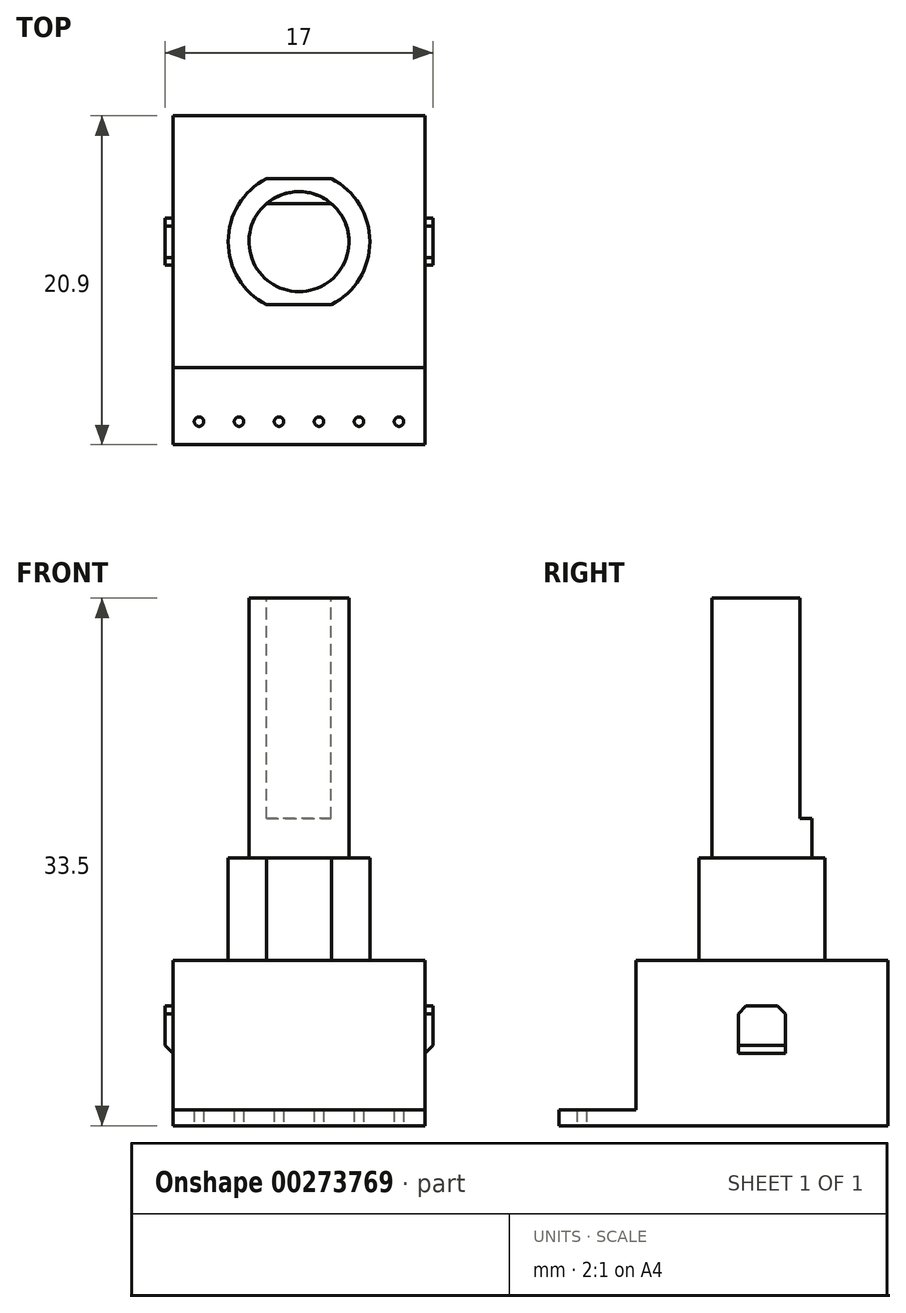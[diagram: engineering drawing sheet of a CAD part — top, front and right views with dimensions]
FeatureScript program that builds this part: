
annotation { "Feature Type Name" : "Feature", "Feature Type Description" : "" }
export const myFeature = defineFeature(function(context is Context, id is Id, definition is map)
    precondition{}
    {
        {
            var Q0;
            Q0=qCreatedBy(makeId("Top.planeOp"),FACE);
            var sketch = newSketch(context, id + "F0", { "sketchPlane" : qUnion([Q0])});
            skLineSegment(sketch, "E0.bottom", {"start": v(-8, 8) * mm, "end": v(8, 8) * mm});
            skLineSegment(sketch, "E0.top", {"start": v(-8, -12.9) * mm, "end": v(8, -12.9) * mm});
            skLineSegment(sketch, "E0.left", {"start": v(-8, 8) * mm, "end": v(-8, -12.9) * mm});
            skLineSegment(sketch, "E0.right", {"start": v(8, 8) * mm, "end": v(8, -12.9) * mm});
            skSolve(sketch);
        }
        {
            var Q0;
            Q0=makeQuery(id+"F0.imprint","IMPRINT",FACE,{"disambiguationData":[TD([[makeQuery(id+"F0.imprint","IMPRINT",EDGE,{"derivedFrom":sQuery(id+"F0.wireOp",EDGE,"E0.bottom")}),-1.0]])]});
            extrude(context, id + "F1", {"entities" : qUnion([Q0]), "depth" : 1 * mm});
        }
        {
            var Q0;
            Q0=makeQuery(id+"F1.opExtrude","CAP_FACE",FACE,{"disambiguationData":[OSD([sQuery(id+"F0.wireOp",EDGE,"E0.bottom"),sQuery(id+"F0.wireOp",EDGE,"E0.top"),sQuery(id+"F0.wireOp",EDGE,"E0.left"),sQuery(id+"F0.wireOp",EDGE,"E0.right")])],"isStart":false});
            var sketch = newSketch(context, id + "F2", { "sketchPlane" : qUnion([Q0])});
            skLineSegment(sketch, "E1.bottom", {"start": v(-8, 8) * mm, "end": v(8, 8) * mm});
            skLineSegment(sketch, "E1.top", {"start": v(-8, -8) * mm, "end": v(8, -8) * mm});
            skLineSegment(sketch, "E1.left", {"start": v(-8, 8) * mm, "end": v(-8, -8) * mm});
            skLineSegment(sketch, "E1.right", {"start": v(8, 8) * mm, "end": v(8, -8) * mm});
            skSolve(sketch);
        }
        {
            var Q0;
            Q0=makeQuery(id+"F2.imprint","IMPRINT",FACE,{"disambiguationData":[TD([[makeQuery(id+"F2.imprint","IMPRINT",EDGE,{"derivedFrom":sQuery(id+"F2.wireOp",EDGE,"E1.bottom")}),-1.0]])]});
            extrude(context, id + "F3", {"entities" : qUnion([Q0]), "operationType" : NewBodyOperationType.ADD, "depth" : 9.5 * mm});
        }
        {
            var Q0;
            Q0=makeQuery(id+"F3.opExtrude","CAP_FACE",FACE,{"disambiguationData":[OSD([sQuery(id+"F2.wireOp",EDGE,"E1.bottom"),sQuery(id+"F2.wireOp",EDGE,"E1.top"),sQuery(id+"F2.wireOp",EDGE,"E1.left"),sQuery(id+"F2.wireOp",EDGE,"E1.right")])],"isStart":false});
            var sketch = newSketch(context, id + "F4", { "sketchPlane" : qUnion([Q0])});
            skArc(sketch, "E2", {"start": v(-2.06, 4) * mm, "mid": v(-4.5, 0) * mm, "end": v(-2.06, -4) * mm});
            skLineSegment(sketch, "E3", {"start": v(-2.06, 4) * mm, "end": v(2.06, 4) * mm});
            skLineSegment(sketch, "E4", {"start": v(2.06, -4) * mm, "end": v(-2.06, -4) * mm});
            skArc(sketch, "E5.trimOffspring", {"start": v(2.06, -4) * mm, "mid": v(4.5, 0) * mm, "end": v(2.06, 4) * mm});
            skSolve(sketch);
        }
        {
            var Q0;
            Q0=makeQuery(id+"F4.imprint","IMPRINT",FACE,{"disambiguationData":[TD([[makeQuery(id+"F4.imprint","IMPRINT",EDGE,{"derivedFrom":sQuery(id+"F4.wireOp",EDGE,"E2")}),1.0]])]});
            extrude(context, id + "F5", {"entities" : qUnion([Q0]), "operationType" : NewBodyOperationType.ADD, "depth" : 6.5 * mm});
        }
        {
            var Q0;
            Q0=makeQuery(id+"F5.opExtrude","CAP_FACE",FACE,{"disambiguationData":[OSD([sQuery(id+"F4.wireOp",EDGE,"E2"),sQuery(id+"F4.wireOp",EDGE,"E3"),sQuery(id+"F4.wireOp",EDGE,"E4"),sQuery(id+"F4.wireOp",EDGE,"E5.trimOffspring")])],"isStart":false});
            var sketch = newSketch(context, id + "F6", { "sketchPlane" : qUnion([Q0])});
            skCircle(sketch, "E6", {"center": v(0, 0) * mm, "radius": 3.17 * mm});
            skSolve(sketch);
        }
        {
            var Q0;
            Q0=makeQuery(id+"F6.imprint","IMPRINT",FACE,{"disambiguationData":[TD([[makeQuery(id+"F6.imprint","IMPRINT",EDGE,{"derivedFrom":sQuery(id+"F6.wireOp",EDGE,"E6")}),1.0]])]});
            extrude(context, id + "F7", {"entities" : qUnion([Q0]), "operationType" : NewBodyOperationType.ADD, "depth" : (23 - 6.5) * mm});
        }
        {
            var Q0;
            Q0=makeQuery(id+"F7.opExtrude","CAP_FACE",FACE,{"disambiguationData":[OSD([sQuery(id+"F6.wireOp",EDGE,"E6")])],"isStart":false});
            var sketch = newSketch(context, id + "F8", { "sketchPlane" : qUnion([Q0])});
            skLineSegment(sketch, "E7", {"start": v(-2.05, 2.43) * mm, "end": v(2.05, 2.43) * mm});
            skArc(sketch, "E8.0", {"start": v(2.05, 2.43) * mm, "mid": v(0, 3.17) * mm, "end": v(-2.05, 2.43) * mm});
            skSolve(sketch);
        }
        {
            var Q0;
            Q0=makeQuery(id+"F8.imprint","IMPRINT",FACE,{"disambiguationData":[TD([[makeQuery(id+"F8.imprint","IMPRINT",EDGE,{"derivedFrom":sQuery(id+"F8.wireOp",EDGE,"E7")}),1.0]])]});
            extrude(context, id + "F9", {"entities" : qUnion([Q0]), "operationType" : NewBodyOperationType.REMOVE, "oppositeDirection" : true, "depth" : 14 * mm});
        }
        {
            var Q0;
            Q0=makeQuery(id+"F1.opExtrude","CAP_FACE",FACE,{"disambiguationData":[OSD([sQuery(id+"F0.wireOp",EDGE,"E0.bottom"),sQuery(id+"F0.wireOp",EDGE,"E0.top"),sQuery(id+"F0.wireOp",EDGE,"E0.left"),sQuery(id+"F0.wireOp",EDGE,"E0.right")])],"isStart":true});
            var sketch = newSketch(context, id + "F10", { "sketchPlane" : qUnion([Q0])});
            skCircle(sketch, "E9", {"center": v(-6.35, 11.43) * mm, "radius": 0.3 * mm});
            skCircle(sketch, "E10.1.0.0", {"center": v(-3.81, 11.43) * mm, "radius": 0.3 * mm});
            skCircle(sketch, "E10.2.0.0", {"center": v(-1.27, 11.43) * mm, "radius": 0.3 * mm});
            skCircle(sketch, "E10.3.0.0", {"center": v(1.27, 11.43) * mm, "radius": 0.3 * mm});
            skCircle(sketch, "E10.4.0.0", {"center": v(3.81, 11.43) * mm, "radius": 0.3 * mm});
            skCircle(sketch, "E10.5.0.0", {"center": v(6.35, 11.43) * mm, "radius": 0.3 * mm});
            skLineSegment(sketch, "E10.direction1", {"start": v(-6.35, 11.43) * mm, "end": v(-3.81, 11.43) * mm, "construction": true});
            skSolve(sketch);
        }
        {
            var Q0;
            Q0 = qSketchRegion(id + "F10", true);
            extrude(context, id + "F11", {"entities" : qUnion([Q0]), "operationType" : NewBodyOperationType.REMOVE, "endBound" : BoundingType.UP_TO_NEXT, "oppositeDirection" : true, "depth" : 6 * mm});
        }
        {
            var Q0;
            Q0=makeQuery(id+"F3.boolean.opBoolean","MERGE",FACE,{"derivedFrom":[makeQuery(id+"F1.opExtrude","SWEPT_FACE",FACE,{"disambiguationData":[OSD([sQuery(id+"F0.wireOp",EDGE,"E0.left")])]}),makeQuery(id+"F3.opExtrude","SWEPT_FACE",FACE,{"disambiguationData":[OSD([sQuery(id+"F2.wireOp",EDGE,"E1.left")])]})]});
            var sketch = newSketch(context, id + "F12", { "sketchPlane" : qUnion([Q0])});
            skLineSegment(sketch, "E11.bottom", {"start": v(1.5, 7.6) * mm, "end": v(-1.5, 7.6) * mm});
            skLineSegment(sketch, "E11.top", {"start": v(1.5, 4.6) * mm, "end": v(-1.5, 4.6) * mm});
            skLineSegment(sketch, "E11.left", {"start": v(1.5, 7.6) * mm, "end": v(1.5, 4.6) * mm});
            skLineSegment(sketch, "E11.right", {"start": v(-1.5, 7.6) * mm, "end": v(-1.5, 4.6) * mm});
            skSolve(sketch);
        }
        {
            var Q0;
            Q0=makeQuery(id+"F12.imprint","IMPRINT",FACE,{"disambiguationData":[TD([[makeQuery(id+"F12.imprint","IMPRINT",EDGE,{"derivedFrom":sQuery(id+"F12.wireOp",EDGE,"E11.bottom")}),1.0]])]});
            extrude(context, id + "F13", {"entities" : qUnion([Q0]), "operationType" : NewBodyOperationType.ADD, "depth" : 0.5 * mm});
        }
        {
            var Q0;
            Q0=makeQuery(id+"F3.boolean.opBoolean","MERGE",FACE,{"derivedFrom":[makeQuery(id+"F1.opExtrude","SWEPT_FACE",FACE,{"disambiguationData":[OSD([sQuery(id+"F0.wireOp",EDGE,"E0.right")])]}),makeQuery(id+"F3.opExtrude","SWEPT_FACE",FACE,{"disambiguationData":[OSD([sQuery(id+"F2.wireOp",EDGE,"E1.right")])]})]});
            var sketch = newSketch(context, id + "F14", { "sketchPlane" : qUnion([Q0])});
            skLineSegment(sketch, "E12.0.0", {"start": v(1.5, 4.6) * mm, "end": v(-1.5, 4.6) * mm});
            skLineSegment(sketch, "E12.0.1", {"start": v(-1.5, 4.6) * mm, "end": v(-1.5, 7.6) * mm});
            skLineSegment(sketch, "E12.0.2", {"start": v(-1.5, 7.6) * mm, "end": v(1.5, 7.6) * mm});
            skLineSegment(sketch, "E12.0.3", {"start": v(1.5, 7.6) * mm, "end": v(1.5, 4.6) * mm});
            skSolve(sketch);
        }
        {
            var Q0;
            Q0=makeQuery(id+"F14.imprint","IMPRINT",FACE,{"disambiguationData":[TD([[makeQuery(id+"F14.imprint","IMPRINT",EDGE,{"derivedFrom":sQuery(id+"F14.wireOp",EDGE,"E12.0.0")}),-1.0]])]});
            extrude(context, id + "F15", {"entities" : qUnion([Q0]), "operationType" : NewBodyOperationType.ADD, "depth" : 0.5 * mm});
        }
        {
            var Q0;
            Q0=makeQuery(id+"F13.opExtrude","SWEPT_EDGE",EDGE,{"disambiguationData":[OSD([sQuery(id+"F12.wireOp",EDGE,"E11.bottom"),sQuery(id+"F12.wireOp",EDGE,"E11.right")])]});
            var Q1;
            Q1=makeQuery(id+"F13.opExtrude","SWEPT_EDGE",EDGE,{"disambiguationData":[OSD([sQuery(id+"F12.wireOp",EDGE,"E11.bottom"),sQuery(id+"F12.wireOp",EDGE,"E11.left")])]});
            chamfer(context, id + "F16", {"entities" : qUnion([Q0, Q1]), "width" : 0.5 * mm, "tangentPropagation" : true});
        }
        {
            var Q0;
            Q0=makeQuery(id+"F13.opExtrude","CAP_EDGE",EDGE,{"disambiguationData":[OSD([sQuery(id+"F12.wireOp",EDGE,"E11.top")])],"isStart":false});
            chamfer(context, id + "F17", {"entities" : qUnion([Q0]), "width" : 0.5 * mm, "tangentPropagation" : true});
        }
        {
            var Q0;
            Q0=makeQuery(id+"F15.opExtrude","CAP_EDGE",EDGE,{"disambiguationData":[OSD([sQuery(id+"F14.wireOp",EDGE,"E12.0.0")])],"isStart":false});
            chamfer(context, id + "F18", {"entities" : qUnion([Q0]), "width" : 0.5 * mm, "tangentPropagation" : true});
        }
        {
            var Q0;
            Q0=makeQuery(id+"F15.opExtrude","SWEPT_EDGE",EDGE,{"disambiguationData":[OSD([sQuery(id+"F14.wireOp",EDGE,"E12.0.2"),sQuery(id+"F14.wireOp",EDGE,"E12.0.3")])]});
            var Q1;
            Q1=makeQuery(id+"F15.opExtrude","SWEPT_EDGE",EDGE,{"disambiguationData":[OSD([sQuery(id+"F14.wireOp",EDGE,"E12.0.1"),sQuery(id+"F14.wireOp",EDGE,"E12.0.2")])]});
            chamfer(context, id + "F19", {"entities" : qUnion([Q0, Q1]), "width" : 0.5 * mm, "tangentPropagation" : true});
        }
    });
